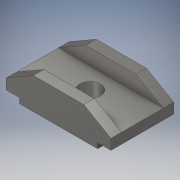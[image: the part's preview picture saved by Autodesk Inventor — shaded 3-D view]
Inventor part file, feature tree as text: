
AUTODESK INVENTOR PART (.ipt)
format: ipt  version: 2019 (Build 230136000, 136)  size: 139,264 bytes
history: native  units: in
note: dims shown in document units (in); Inventor stores cm internally (conversion verified against a paired STEP export)
features: extrude x3, sketch x3, chamfer x2, projected_geometry x1
ambient origin geometry x8: Origin, YZ Plane, XZ Plane, XY Plane, X Axis, Y Axis, Z Axis, Center Point
bodies: Solid1 (feature_tree)
feature tree (9):
  extrude  "Extrusion1"  Depth=1.5in
  chamfer  "Chamfer5"  Distance=0.25in
  chamfer  "Chamfer6"  Distance=0.25in
  extrude  "Extrusion5"  Depth=3.0in TaperAngle=0.0deg
  extrude  "Extrusion6"  Depth=0.75in TaperAngle=60.0deg
  sketch  "Sketch1"  dims[d0=5.0in d1=1.5in]
  sketch  "Sketch8"  dims[d2=0.635in]
  sketch  "Sketch9"  dims[d3=0.635in d4=0.25in d5=0.25in d6=3.0in d7=0.0in d31=0.75in d32=0.125in d33=60.0deg d34=0.75in d35=0.125in d36=60.0deg d37=0.5in d38=0.5in d39=10.0in d40=0.0in d41=1.0in d42=10.0in d43=0.0in]
  projected_geometry  "Projected Loop3"
